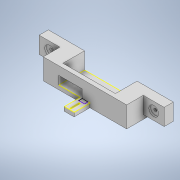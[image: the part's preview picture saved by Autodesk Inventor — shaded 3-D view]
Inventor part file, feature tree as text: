
AUTODESK INVENTOR PART (.ipt)
format: ipt  version: 2020 (Build 240168000, 168)  size: 229,888 bytes
history: native  units: mm
features: extrude x7, sketch x7, projected_geometry x5, mirror x2
ambient origin geometry x8: Origin, YZ Plane, XZ Plane, XY Plane, X Axis, Y Axis, Z Axis, Center Point
bodies: Solid1 (feature_tree)
feature tree (21):
  extrude  "Extrusion1"  Depth=50.0mm
  sketch  "Sketch2"  dims[d2=31.0mm d3=15.5mm]
  extrude  "Extrusion2"  Depth=31.0mm
  extrude  "Extrusion3"  Depth=63.0mm
  mirror  "Mirror1"
  extrude  "Extrusion5"  Depth=11.0mm
  extrude  "Extrusion6"  Depth=20.0mm TaperAngle=0.0deg
  extrude  "Extrusion7"  Depth=11.5mm
  extrude  "Extrusion8"  Depth=2.0mm TaperAngle=0.0deg
  mirror  "Mirror2"
  sketch  "Sketch10"  dims[d13=0.0mm d14=0.0mm d15=2.0mm d16=0.0mm d22=100.0mm d23=50.0mm d24=5.0mm d25=0.0mm d26=28.0mm d27=10.0mm d28=57.0mm d29=0.0mm d30=2.0mm d31=0.0mm d32=5.0mm d33=24.25mm d34=0.0mm d36=10.0mm d37=2.0mm d38=0.5mm d39=0.872665mm]
  sketch  "Sketch1"  dims[d0=100.0mm d1=50.0mm]
  projected_geometry  "Projected Loop1"
  sketch  "Sketch4"  dims[d4=26.0mm d5=63.0mm]
  projected_geometry  "Projected Loop3"
  sketch  "Sketch5"  dims[d6=31.5mm d7=11.0mm]
  sketch  "Sketch6"  dims[d8=25.0mm d9=20.0mm d10=0.0mm]
  projected_geometry  "Projected Loop4"
  sketch  "Sketch7"  dims[d11=3.5mm d12=11.5mm]
  projected_geometry  "Projected Loop5"
  projected_geometry  "Projected Loop10"
